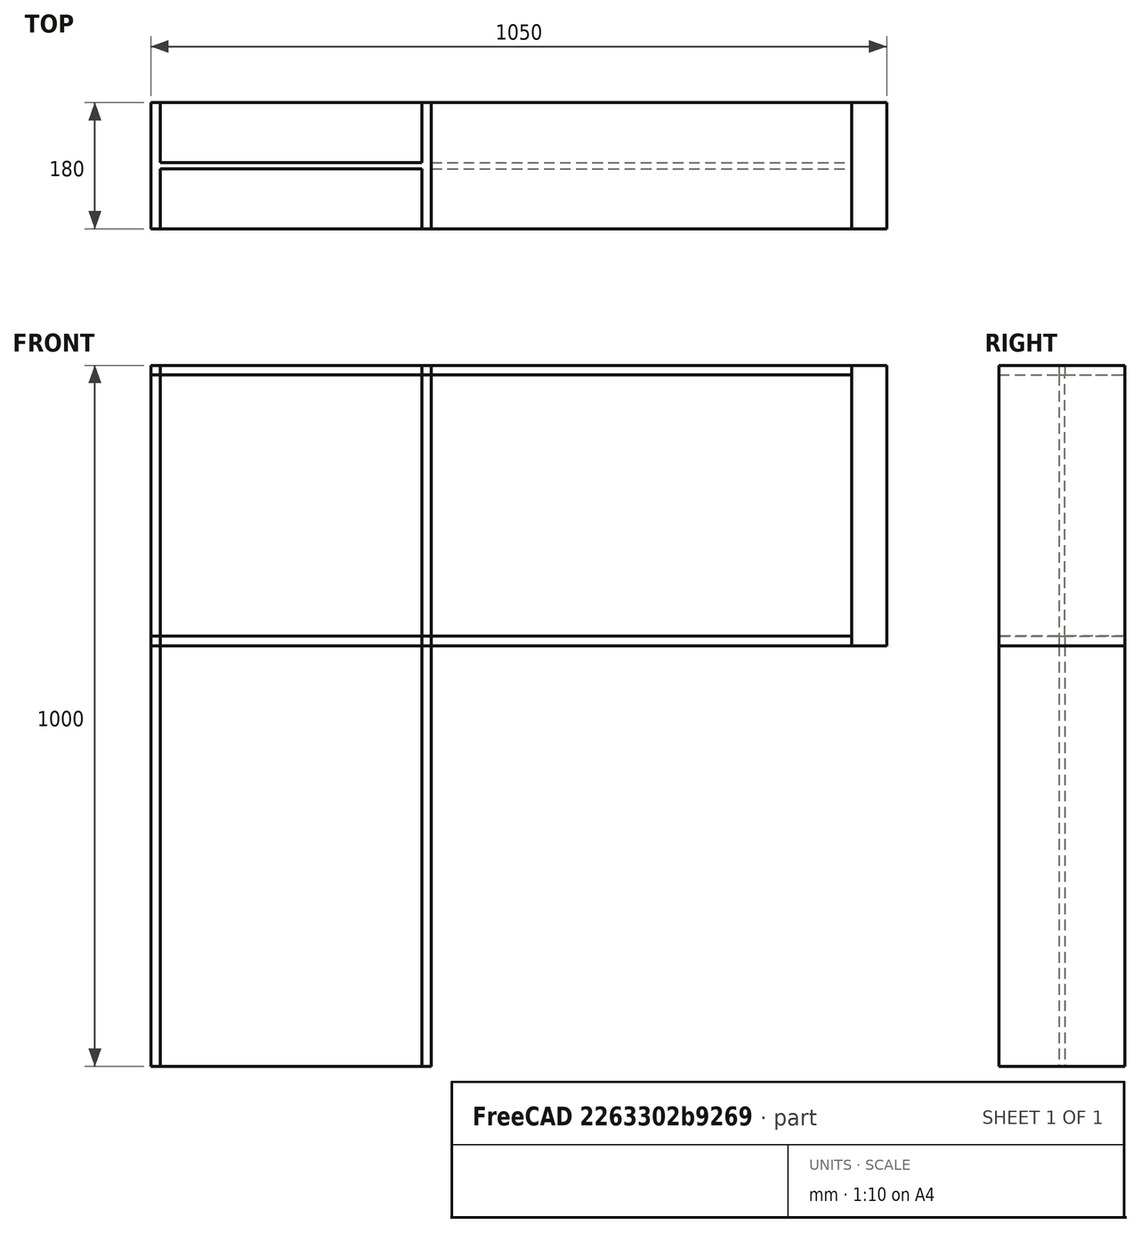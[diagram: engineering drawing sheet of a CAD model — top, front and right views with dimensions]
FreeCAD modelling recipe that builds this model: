
FCSTD DOCUMENT  (FreeCAD 0.21R33771 (Git))
Label: IPE400_2
License: All rights reserved
LicenseURL: http://en.wikipedia.org/wiki/All_rights_reserved
objects: Part::Box×3, Sketcher::SketchObject×2, Part::Extrusion×2, Fem::ConstraintForce×2, App::MaterialObjectPython×1, Fem::FemSolverObjectPython×1, Part::FeaturePython×1, Fem::ConstraintFixed×1, Fem::ConstraintDisplacement×1, Fem::FemMeshObjectPython×1, Fem::FemAnalysis×1
note: 8 computed .brp shape members not serialized (recipe doc carries the construction recipe); baked Part::Feature solids carry a one-line shape summary decoded from their .brp

FEATURE [Sketcher::SketchObject] Sketch
  FullyConstrained = true
  Placement = pos=(0,0,0) rot=(0.57735,0.57735,0.57735;2.0944rad)
  sketch-geometry (12):
    g0: LineSegment StartX=0 StartY=0 StartZ=0 EndX=180 EndY=0 EndZ=0
    g1: LineSegment StartX=180 StartY=0 StartZ=0 EndX=180 EndY=13.5 EndZ=0
    g2: LineSegment StartX=180 StartY=13.5 StartZ=0 EndX=94.3 EndY=13.5 EndZ=0
    g3: LineSegment StartX=94.3 StartY=13.5 StartZ=0 EndX=94.3 EndY=386.5 EndZ=0
    g4: LineSegment StartX=94.3 StartY=386.5 StartZ=0 EndX=180 EndY=386.5 EndZ=0
    g5: LineSegment StartX=180 StartY=386.5 StartZ=0 EndX=180 EndY=400 EndZ=0
    g6: LineSegment StartX=180 StartY=400 StartZ=0 EndX=0 EndY=400 EndZ=0
    g7: LineSegment StartX=0 StartY=400 StartZ=0 EndX=0 EndY=386.5 EndZ=0
    g8: LineSegment StartX=0 StartY=386.5 StartZ=0 EndX=85.7 EndY=386.5 EndZ=0
    g9: LineSegment StartX=85.7 StartY=386.5 StartZ=0 EndX=85.7 EndY=13.5 EndZ=0
    g10: LineSegment StartX=85.7 StartY=13.5 StartZ=0 EndX=0 EndY=13.5 EndZ=0
    g11: LineSegment StartX=0 StartY=13.5 StartZ=0 EndX=0 EndY=0 EndZ=0
  constraints (35):
    c: Coincident(g-1,g0)
    c: PointOnObject(g0,g-1)
    c: Coincident(g0,g1)
    c: Vertical(g1)
    c: Coincident(g1,g2)
    c: Horizontal(g2)
    c: Coincident(g2,g3)
    c: Vertical(g3)
    c: Coincident(g3,g4)
    c: Horizontal(g4)
    c: Coincident(g4,g5)
    c: Vertical(g5)
    c: Coincident(g5,g6)
    c: Horizontal(g6)
    c: Coincident(g6,g7)
    c: Vertical(g7)
    c: Coincident(g7,g8)
    c: Horizontal(g8)
    c: Coincident(g8,g9)
    c: Vertical(g9)
    c: Coincident(g9,g10)
    c: Horizontal(g10)
    c: Coincident(g10,g11)
    c: Coincident(g11,g0)
    c: DistanceX(g0,g0) = 180
    c: DistanceX(g6,g6) = 180
    c: PointOnObject(g6,g-2)
    c: Vertical(g11)
    c: DistanceX(g2,g2) = 85.7
    c: Equal(g10,g2)
    c: DistanceY(g11,g11) = 13.5
    c: Equal(g11,g1)
    c: Equal(g11,g7)
    c: Equal(g11,g5)
    c: DistanceY(g0,g6) = 400
FEATURE [Part::Extrusion] Extrude
  Base = -> Sketch
  Dir = (1,0,0)
  DirMode = 2
  FaceMakerClass = Part::FaceMakerBullseye
  LengthFwd = 600
  LengthRev = 0
  Solid = true
  Symmetric = false
FEATURE [Sketcher::SketchObject] Sketch001
  FullyConstrained = true
  Placement = pos=(0,0,0) rot=(0.57735,0.57735,0.57735;2.0944rad)
  sketch-geometry (12):
    g0: LineSegment StartX=0 StartY=0 StartZ=0 EndX=180 EndY=0 EndZ=0
    g1: LineSegment StartX=180 StartY=0 StartZ=0 EndX=180 EndY=13.5 EndZ=0
    g2: LineSegment StartX=180 StartY=13.5 StartZ=0 EndX=94.3 EndY=13.5 EndZ=0
    g3: LineSegment StartX=94.3 StartY=13.5 StartZ=0 EndX=94.3 EndY=386.5 EndZ=0
    g4: LineSegment StartX=94.3 StartY=386.5 StartZ=0 EndX=180 EndY=386.5 EndZ=0
    g5: LineSegment StartX=180 StartY=386.5 StartZ=0 EndX=180 EndY=400 EndZ=0
    g6: LineSegment StartX=180 StartY=400 StartZ=0 EndX=0 EndY=400 EndZ=0
    g7: LineSegment StartX=0 StartY=400 StartZ=0 EndX=0 EndY=386.5 EndZ=0
    g8: LineSegment StartX=0 StartY=386.5 StartZ=0 EndX=85.7 EndY=386.5 EndZ=0
    g9: LineSegment StartX=85.7 StartY=386.5 StartZ=0 EndX=85.7 EndY=13.5 EndZ=0
    g10: LineSegment StartX=85.7 StartY=13.5 StartZ=0 EndX=0 EndY=13.5 EndZ=0
    g11: LineSegment StartX=0 StartY=13.5 StartZ=0 EndX=0 EndY=0 EndZ=0
  constraints (35):
    c: Coincident(g-1,g0)
    c: PointOnObject(g0,g-1)
    c: Coincident(g0,g1)
    c: Vertical(g1)
    c: Coincident(g1,g2)
    c: Horizontal(g2)
    c: Coincident(g2,g3)
    c: Vertical(g3)
    c: Coincident(g3,g4)
    c: Horizontal(g4)
    c: Coincident(g4,g5)
    c: Vertical(g5)
    c: Coincident(g5,g6)
    c: Horizontal(g6)
    c: Coincident(g6,g7)
    c: Vertical(g7)
    c: Coincident(g7,g8)
    c: Horizontal(g8)
    c: Coincident(g8,g9)
    c: Vertical(g9)
    c: Coincident(g9,g10)
    c: Horizontal(g10)
    c: Coincident(g10,g11)
    c: Coincident(g11,g0)
    c: DistanceX(g0,g0) = 180
    c: DistanceX(g6,g6) = 180
    c: PointOnObject(g6,g-2)
    c: Vertical(g11)
    c: DistanceX(g2,g2) = 85.7
    c: Equal(g10,g2)
    c: DistanceY(g11,g11) = 13.5
    c: Equal(g11,g1)
    c: Equal(g11,g7)
    c: Equal(g11,g5)
    c: DistanceY(g0,g6) = 400
FEATURE [Part::Extrusion] Extrude001
  Base = -> Sketch001
  Dir = (1,0,0)
  DirMode = 2
  FaceMakerClass = Part::FaceMakerBullseye
  LengthFwd = 1000
  LengthRev = 0
  Placement = pos=(-400,0,400) rot=(0,1,0;1.5708rad)
  Solid = true
  Symmetric = false
FEATURE [Part::Box] Box  label="Cube"
  AttacherType = Attacher::AttachEngine3D
  Height = 400
  Length = 50
  Placement = pos=(600,0,0) rot=(0,0,1;0rad)
  Width = 180
FEATURE [App::MaterialObjectPython] MaterialSolid  # material (typed FeaturePython)
  Category = 0
  Material = AuthorAndLicense=(c) 2014 M. Münch - GNU Lesser General Public License (LGPL),CardName=Steel-15CrNi6,Density=7800 kg/m^3,+16 more (map truncated)
FEATURE [Fem::FemSolverObjectPython] SolverCcxTools  # FEM object (typed FeaturePython)
  AnalysisType = 0
  BeamShellResultOutput3D = false
  BucklingFactors = 1
  EigenmodeHighLimit = 1000000
  EigenmodeLowLimit = 0
  EigenmodesCount = 10
  GeometricalNonlinearity = 0
  IterationsControlParameterCutb = 0.25,0.5,0.75,0.85,,,1.5,
  IterationsControlParameterIter = 4,8,9,200,10,400,,200,,
  IterationsControlParameterTimeUse = false
  IterationsThermoMechMaximum = 2000
  IterationsUserDefinedIncrementations = false
  IterationsUserDefinedTimeStepLength = false
  MaterialNonlinearity = 0
  MatrixSolverType = 0
  SplitInputWriter = false
  ThermoMechSteadyState = true
  TimeEnd = 1
  TimeInitialStep = 0.01
FEATURE [Part::Box] Box001  label="Cube001"
  AttacherType = Attacher::AttachEngine3D
  Height = 13.5
  Length = 400
  Placement = pos=(-400,0,0) rot=(0,0,1;0rad)
  Width = 180
FEATURE [Part::Box] Box002  label="Cube002"
  AttacherType = Attacher::AttachEngine3D
  Height = 13.5
  Length = 400
  Placement = pos=(-400,0,386.5) rot=(0,0,1;0rad)
  Width = 180
FEATURE [Part::FeaturePython] BooleanFragments  # WARN: FeaturePython — macro-defined, semantics opaque (R4)
  Mode = 2
  Objects = -> [Extrude,Extrude001,Box,Box001,Box002]
  Tolerance = 0
FEATURE [Fem::ConstraintForce] ConstraintForce
  Direction = -> BooleanFragments [Edge146]
  DirectionVector = (1,0,0)
  Force = 1000000
  NormalDirection = (0,0,1)
  Points = (16) [(600,0,400),(616.667,0,400),(633.333,0,400),(650,0,400),(600,60,400),(616.667,60,400),(633.333,60,400),(650,60,400),(600,120,400),(616.667,120,400),+6 more]
  References = -> [BooleanFragments]
  Scale = 11
FEATURE [Fem::ConstraintFixed] ConstraintFixed
  NormalDirection = (0,0,-1)
  Normals = (8) [(0,0,-1),(0,0,-1),(0,0,-1),(0,0,-1),(0,0,-1),(0,0,-1),(0,0,-1),(0,0,-1)]
  Points = (8) [(-400,180,-600),(0,180,-600),(-400,120,-600),(0,120,-600),(-400,60,-600),(0,60,-600),(-400,0,-600),(0,0,-600)]
  References = -> [BooleanFragments]
  Scale = 18
FEATURE [Fem::ConstraintForce] ConstraintForce001
  Direction = -> BooleanFragments [Edge145]
  DirectionVector = (-1,0,0)
  Force = 1000000
  NormalDirection = (0,0,-1)
  Points = (16) [(600,0,0),(616.667,0,0),(633.333,0,0),(650,0,0),(600,60,0),(616.667,60,0),(633.333,60,0),(650,60,0),(600,120,0),(616.667,120,0),(633.333,120,0),+5 more]
  References = -> [BooleanFragments]
  Reversed = true
  Scale = 11
FEATURE [Fem::ConstraintDisplacement] ConstraintDisplacement
  NormalDirection = (0,1,0)
  Normals = (16) [(0,1,0),(0,1,0),(0,1,0),(0,1,0),(0,1,0),(0,1,0),(0,1,0),(0,1,0),(0,1,0),(0,1,0),(0,1,0),(0,1,0),(0,1,0),(0,1,0),(0,1,0),(0,1,0)]
  Points = (16) [(600,180,0),(600,180,133.333),(600,180,266.667),(600,180,400),(616.667,180,0),(616.667,180,133.333),(616.667,180,266.667),(616.667,180,400),+8 more]
  References = -> [BooleanFragments]
  Scale = 16
  hasXFormula = false
  hasYFormula = false
  hasZFormula = false
  rotxFix = false
  rotxFree = true
  rotyFix = false
  rotyFree = true
  rotzFix = false
  rotzFree = true
  useFlowSurfaceForce = false
  xDisplacement = 0
  xFix = false
  xFree = true
  xRotation = 0
  yDisplacement = 0
  yFix = false
  yFree = false
  yRotation = 0
  zDisplacement = 0
  zFix = false
  zFree = true
  zRotation = 0
FEATURE [Fem::FemMeshObjectPython] FEMMeshGmsh  # FEM object (typed FeaturePython)
  Algorithm2D = 0
  Algorithm3D = 0
  CharacteristicLengthMax = 25
  CharacteristicLengthMin = 0
  CoherenceMesh = true
  ElementDimension = 0
  ElementOrder = 1
  GeometryTolerance = 1e-06
  GroupsOfNodes = false
  HighOrderOptimize = 0
  MeshSizeFromCurvature = 12
  OptimizeNetgen = false
  OptimizeStd = true
  Part = -> BooleanFragments
  RecombinationAlgorithm = 0
  Recombine3DAll = false
  RecombineAll = false
  SecondOrderLinear = false
FEATURE [Fem::FemAnalysis] Analysis
  Group = -> [ConstraintForce,ConstraintFixed,MaterialSolid,ConstraintForce001,SolverCcxTools,ConstraintDisplacement,FEMMeshGmsh]
